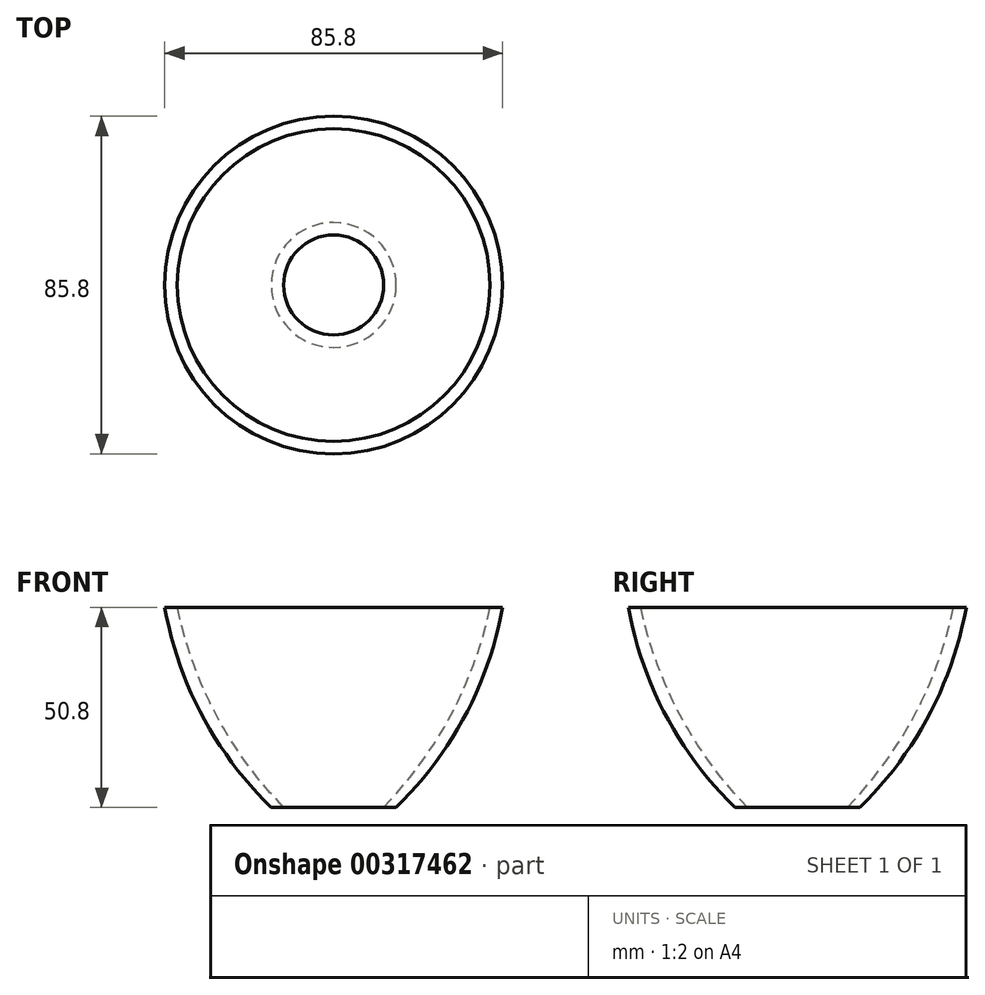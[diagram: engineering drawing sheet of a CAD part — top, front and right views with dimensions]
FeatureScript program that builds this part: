
annotation { "Feature Type Name" : "Feature", "Feature Type Description" : "" }
export const myFeature = defineFeature(function(context is Context, id is Id, definition is map)
    precondition{}
    {
        {
            var Q0;
            Q0=qCreatedBy(makeId("Front.planeOp"),FACE);
            var sketch = newSketch(context, id + "F0", { "sketchPlane" : qUnion([Q0])});
            skArc(sketch, "E0", {"start": v(-39.72, 50.8) * mm, "mid": v(-29.82, 23.48) * mm, "end": v(-12.7, 0) * mm});
            skPoint(sketch, "E1.end.orphan", {"position": v(0, 50.8) * mm});
            skLineSegment(sketch, "E2", {"start": v(0, 0) * mm, "end": v(0, 50.8) * mm});
            skPoint(sketch, "E3.end.orphan", {"position": v(-20.99, 0) * mm});
            skPoint(sketch, "E3.start.orphan", {"position": v(-47.4, 50.8) * mm});
            skPoint(sketch, "E4.end.orphan", {"position": v(-24.15, 0) * mm});
            skPoint(sketch, "E4.start.orphan", {"position": v(-50.78, 50.8) * mm});
            skLineSegment(sketch, "E5", {"start": v(-12.7, 0) * mm, "end": v(-15.87, 0) * mm});
            skLineSegment(sketch, "E6", {"start": v(-39.72, 50.8) * mm, "end": v(-42.9, 50.8) * mm});
            skArc(sketch, "E7", {"start": v(-42.9, 50.8) * mm, "mid": v(-33.37, 23.28) * mm, "end": v(-15.88, 0) * mm});
            skSolve(sketch);
        }
        {
            var Q0;
            Q0 = qSketchRegion(id + "F0", true);
            var Q1;
            Q1=sQuery(id+"F0.wireOp",EDGE,"E2");
            revolve(context, id + "F1", {"entities" : qUnion([Q0]), "axis" : qUnion([Q1]), "revolveType" : RevolveType.FULL});
        }
    });
